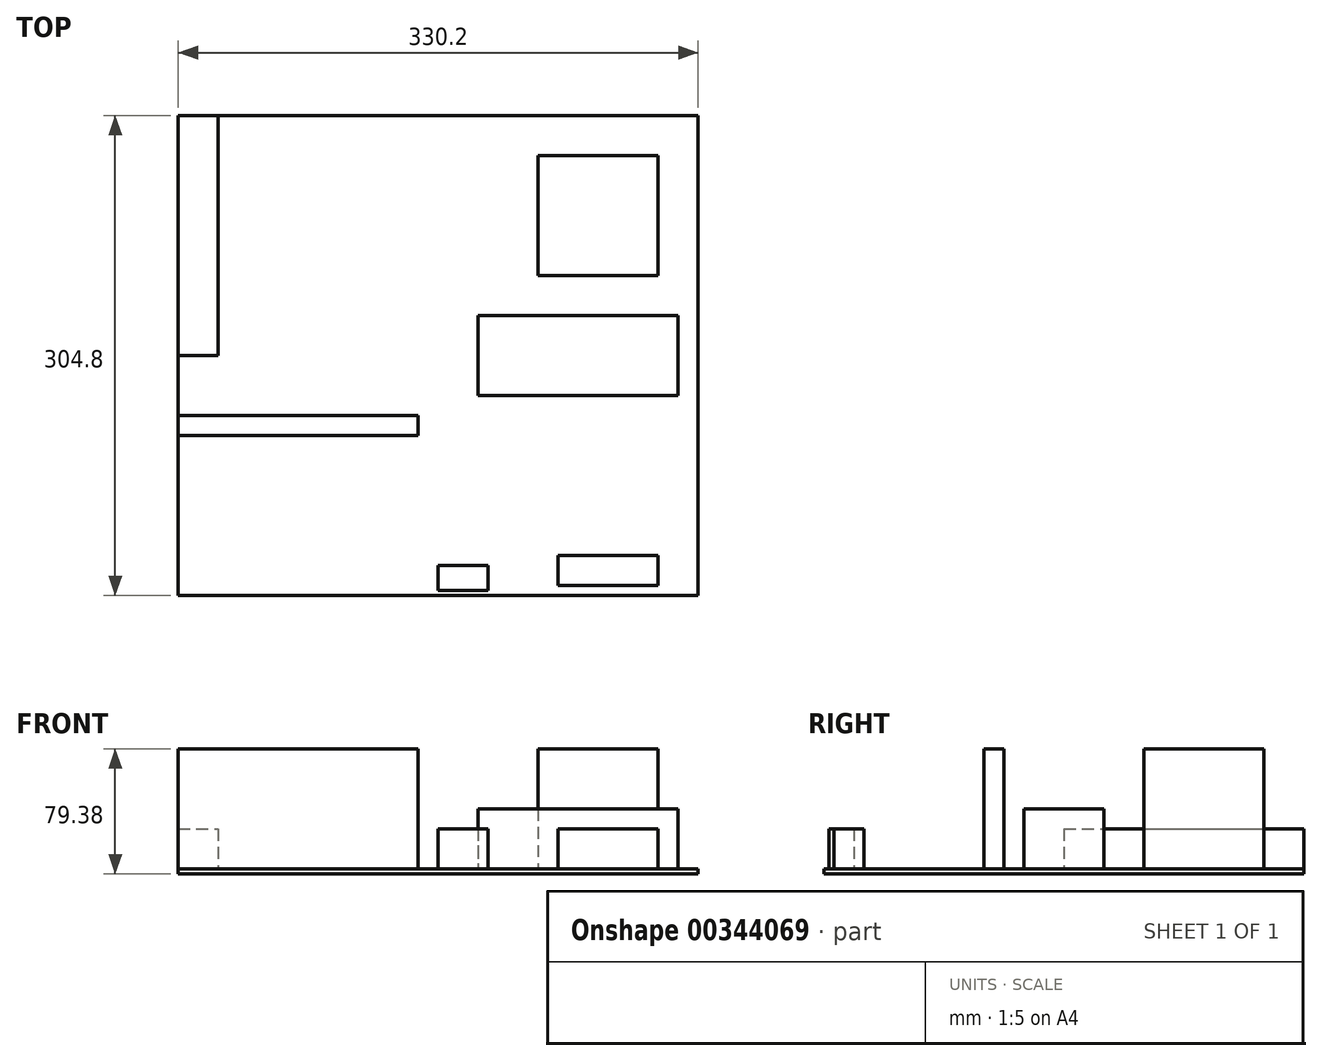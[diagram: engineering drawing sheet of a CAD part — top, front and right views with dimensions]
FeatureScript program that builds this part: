
annotation { "Feature Type Name" : "Feature", "Feature Type Description" : "" }
export const myFeature = defineFeature(function(context is Context, id is Id, definition is map)
    precondition{}
    {
        {
            var Q0;
            Q0=qCreatedBy(makeId("Top.planeOp"),FACE);
            var sketch = newSketch(context, id + "F0", { "sketchPlane" : qUnion([Q0])});
            skLineSegment(sketch, "E0.bottom", {"start": v(0, 0) * mm, "end": v(330.2, 0) * mm});
            skLineSegment(sketch, "E0.top", {"start": v(0, 304.8) * mm, "end": v(330.2, 304.8) * mm});
            skLineSegment(sketch, "E0.left", {"start": v(0, 0) * mm, "end": v(0, 304.8) * mm});
            skLineSegment(sketch, "E0.right", {"start": v(330.2, 0) * mm, "end": v(330.2, 304.8) * mm});
            skSolve(sketch);
        }
        {
            var Q0;
            Q0=makeQuery(id+"F0.imprint","IMPRINT",FACE,{"disambiguationData":[TD([[makeQuery(id+"F0.imprint","IMPRINT",EDGE,{"derivedFrom":sQuery(id+"F0.wireOp",EDGE,"E0.bottom")}),1.0]])]});
            extrude(context, id + "F1", {"entities" : qUnion([Q0]), "depth" : 3.17 * mm});
        }
        {
            var Q0;
            Q0=makeQuery(id+"F1.opExtrude","CAP_FACE",FACE,{"disambiguationData":[OSD([sQuery(id+"F0.wireOp",EDGE,"E0.bottom"),sQuery(id+"F0.wireOp",EDGE,"E0.top"),sQuery(id+"F0.wireOp",EDGE,"E0.left"),sQuery(id+"F0.wireOp",EDGE,"E0.right")])],"isStart":false});
            var sketch = newSketch(context, id + "F2", { "sketchPlane" : qUnion([Q0])});
            skLineSegment(sketch, "E1.bottom", {"start": v(228.6, 279.4) * mm, "end": v(304.8, 279.4) * mm});
            skLineSegment(sketch, "E1.top", {"start": v(228.6, 203.2) * mm, "end": v(304.8, 203.2) * mm});
            skLineSegment(sketch, "E1.left", {"start": v(228.6, 279.4) * mm, "end": v(228.6, 203.2) * mm});
            skLineSegment(sketch, "E1.right", {"start": v(304.8, 279.4) * mm, "end": v(304.8, 203.2) * mm});
            skSolve(sketch);
        }
        {
            var Q0;
            Q0=makeQuery(id+"F2.imprint","IMPRINT",FACE,{"disambiguationData":[TD([[makeQuery(id+"F2.imprint","IMPRINT",EDGE,{"derivedFrom":sQuery(id+"F2.wireOp",EDGE,"E1.bottom")}),-1.0]])]});
            extrude(context, id + "F3", {"entities" : qUnion([Q0]), "operationType" : NewBodyOperationType.ADD, "depth" : 76.2 * mm});
        }
        {
            var Q0;
            Q0=makeQuery(id+"F1.opExtrude","CAP_FACE",FACE,{"disambiguationData":[OSD([sQuery(id+"F0.wireOp",EDGE,"E0.bottom"),sQuery(id+"F0.wireOp",EDGE,"E0.top"),sQuery(id+"F0.wireOp",EDGE,"E0.left"),sQuery(id+"F0.wireOp",EDGE,"E0.right")])],"isStart":false});
            var sketch = newSketch(context, id + "F4", { "sketchPlane" : qUnion([Q0])});
            skLineSegment(sketch, "E2.bottom", {"start": v(0, 152.4) * mm, "end": v(25.4, 152.4) * mm});
            skLineSegment(sketch, "E2.top", {"start": v(0, 304.8) * mm, "end": v(25.4, 304.8) * mm});
            skLineSegment(sketch, "E2.left", {"start": v(0, 152.4) * mm, "end": v(0, 304.8) * mm});
            skLineSegment(sketch, "E2.right", {"start": v(25.4, 152.4) * mm, "end": v(25.4, 304.8) * mm});
            skSolve(sketch);
        }
        {
            var Q0;
            Q0 = qSketchRegion(id + "F4", true);
            extrude(context, id + "F5", {"entities" : qUnion([Q0]), "operationType" : NewBodyOperationType.ADD, "depth" : 25.4 * mm});
        }
        {
            var Q0;
            Q0=makeQuery(id+"F1.opExtrude","CAP_FACE",FACE,{"disambiguationData":[OSD([sQuery(id+"F0.wireOp",EDGE,"E0.bottom"),sQuery(id+"F0.wireOp",EDGE,"E0.top"),sQuery(id+"F0.wireOp",EDGE,"E0.left"),sQuery(id+"F0.wireOp",EDGE,"E0.right")])],"isStart":false});
            var sketch = newSketch(context, id + "F6", { "sketchPlane" : qUnion([Q0])});
            skLineSegment(sketch, "E3.bottom", {"start": v(0, 101.6) * mm, "end": v(152.4, 101.6) * mm});
            skLineSegment(sketch, "E3.top", {"start": v(0, 114.3) * mm, "end": v(152.4, 114.3) * mm});
            skLineSegment(sketch, "E3.left", {"start": v(0, 101.6) * mm, "end": v(0, 114.3) * mm});
            skLineSegment(sketch, "E3.right", {"start": v(152.4, 101.6) * mm, "end": v(152.4, 114.3) * mm});
            skSolve(sketch);
        }
        {
            var Q0;
            Q0=makeQuery(id+"F6.imprint","IMPRINT",FACE,{"disambiguationData":[TD([[makeQuery(id+"F6.imprint","IMPRINT",EDGE,{"derivedFrom":sQuery(id+"F6.wireOp",EDGE,"E3.bottom")}),1.0]])]});
            extrude(context, id + "F7", {"entities" : qUnion([Q0]), "operationType" : NewBodyOperationType.ADD, "depth" : 76.2 * mm});
        }
        {
            var Q0;
            Q0=makeQuery(id+"F1.opExtrude","CAP_FACE",FACE,{"disambiguationData":[OSD([sQuery(id+"F0.wireOp",EDGE,"E0.bottom"),sQuery(id+"F0.wireOp",EDGE,"E0.top"),sQuery(id+"F0.wireOp",EDGE,"E0.left"),sQuery(id+"F0.wireOp",EDGE,"E0.right")])],"isStart":false});
            var sketch = newSketch(context, id + "F8", { "sketchPlane" : qUnion([Q0])});
            skLineSegment(sketch, "E4.bottom", {"start": v(190.5, 177.8) * mm, "end": v(317.5, 177.8) * mm});
            skLineSegment(sketch, "E4.top", {"start": v(190.5, 127) * mm, "end": v(317.5, 127) * mm});
            skLineSegment(sketch, "E4.left", {"start": v(190.5, 177.8) * mm, "end": v(190.5, 127) * mm});
            skLineSegment(sketch, "E4.right", {"start": v(317.5, 177.8) * mm, "end": v(317.5, 127) * mm});
            skSolve(sketch);
        }
        {
            var Q0;
            Q0 = qSketchRegion(id + "F8", true);
            extrude(context, id + "F9", {"entities" : qUnion([Q0]), "operationType" : NewBodyOperationType.ADD, "depth" : 38.1 * mm});
        }
        {
            var Q0;
            Q0=makeQuery(id+"F1.opExtrude","CAP_FACE",FACE,{"disambiguationData":[OSD([sQuery(id+"F0.wireOp",EDGE,"E0.bottom"),sQuery(id+"F0.wireOp",EDGE,"E0.top"),sQuery(id+"F0.wireOp",EDGE,"E0.left"),sQuery(id+"F0.wireOp",EDGE,"E0.right")])],"isStart":false});
            var sketch = newSketch(context, id + "F10", { "sketchPlane" : qUnion([Q0])});
            skLineSegment(sketch, "E5.bottom", {"start": v(241.3, 25.4) * mm, "end": v(304.8, 25.4) * mm});
            skLineSegment(sketch, "E5.top", {"start": v(241.3, 6.35) * mm, "end": v(304.8, 6.35) * mm});
            skLineSegment(sketch, "E5.left", {"start": v(241.3, 25.4) * mm, "end": v(241.3, 6.35) * mm});
            skLineSegment(sketch, "E5.right", {"start": v(304.8, 25.4) * mm, "end": v(304.8, 6.35) * mm});
            skSolve(sketch);
        }
        {
            var Q0;
            Q0 = qSketchRegion(id + "F10", true);
            extrude(context, id + "F11", {"entities" : qUnion([Q0]), "operationType" : NewBodyOperationType.ADD, "depth" : 25.4 * mm});
        }
        {
            var Q0;
            Q0=makeQuery(id+"F1.opExtrude","CAP_FACE",FACE,{"disambiguationData":[OSD([sQuery(id+"F0.wireOp",EDGE,"E0.bottom"),sQuery(id+"F0.wireOp",EDGE,"E0.top"),sQuery(id+"F0.wireOp",EDGE,"E0.left"),sQuery(id+"F0.wireOp",EDGE,"E0.right")])],"isStart":false});
            var sketch = newSketch(context, id + "F12", { "sketchPlane" : qUnion([Q0])});
            skLineSegment(sketch, "E6.bottom", {"start": v(165.1, 19.05) * mm, "end": v(196.85, 19.05) * mm});
            skLineSegment(sketch, "E6.top", {"start": v(165.1, 3.18) * mm, "end": v(196.85, 3.18) * mm});
            skLineSegment(sketch, "E6.left", {"start": v(165.1, 19.05) * mm, "end": v(165.1, 3.17) * mm});
            skLineSegment(sketch, "E6.right", {"start": v(196.85, 19.05) * mm, "end": v(196.85, 3.18) * mm});
            skSolve(sketch);
        }
        {
            var Q0;
            Q0 = qSketchRegion(id + "F12", true);
            extrude(context, id + "F13", {"entities" : qUnion([Q0]), "operationType" : NewBodyOperationType.ADD, "depth" : 25.4 * mm});
        }
    });
